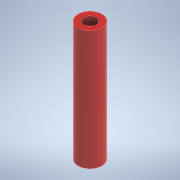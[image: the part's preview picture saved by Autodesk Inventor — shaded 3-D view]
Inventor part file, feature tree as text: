
AUTODESK INVENTOR PART (.ipt)
format: ipt  version: 2021 (Build 250183000, 183)  size: 102,912 bytes
history: native  units: mm
features: sketch x2, revolve x1, hole x1
ambient origin geometry x8: Origin, YZ Plane, XZ Plane, XY Plane, X Axis, Y Axis, Z Axis, Center Point
bodies: Solid1 (feature_tree)
feature tree (4):
  revolve  "Revolution1"  [1 undecoded]
  hole  "Hole1"  [1 undecoded]
  sketch  "Sketch1"  dims[d0=0.0mm d1=15.0mm]
  sketch  "Sketch2"  dims[d2=150.0mm d3=90.0deg d4=16.0mm d5=6.0mm d6=4.0mm d7=2.0mm d8=90.0deg d9=8.0mm d10=20.594885mm]
note: 2 required parameter values undecoded (feature->parameter linkage not recoverable at this tier; creation-order binding heuristic only, values carry confidence <= 0.55)